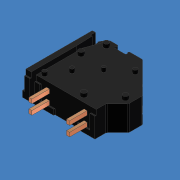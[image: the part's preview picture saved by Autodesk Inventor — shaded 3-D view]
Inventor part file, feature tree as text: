
AUTODESK INVENTOR PART (.ipt)
format: ipt  version: 2012 (Build 160160000, 160)  size: 268,800 bytes
history: native  units: mm (DEFAULTED — no unit token found)
features: sketch x21, extrude x18, revolve x2, pattern_linear x2
ambient origin geometry x8: Origin, YZ Plane, XZ Plane, XY Plane, X Axis, Y Axis, Z Axis, Center Point
bodies: Solid1 (feature_tree)
feature tree (43):
  extrude  "Extrusion1"  Depth=10.0mm TaperAngle=0.0deg
  extrude  "Extrusion2"  Depth=8.8mm TaperAngle=0.0deg
  extrude  "Extrusion3"  Depth=1.5mm TaperAngle=0.0deg
  extrude  "Extrusion4"  Depth=1.5mm TaperAngle=0.0deg
  extrude  "Extrusion5"  Depth=1.5mm TaperAngle=0.0deg
  extrude  "Extrusion6"  Depth=1.5mm TaperAngle=0.0deg
  extrude  "Extrusion7"  Depth=6.3mm TaperAngle=0.0deg
  extrude  "Extrusion8"  TaperAngle=360.0deg  [1 undecoded]
  extrude  "Extrusion9"  TaperAngle=360.0deg  [1 undecoded]
  extrude  "Extrusion10"  Depth=20.0mm TaperAngle=0.0deg
  extrude  "Extrusion11"  Depth=20.0mm TaperAngle=0.0deg
  extrude  "Extrusion12"  [1 undecoded]
  extrude  "Extrusion13"  [1 undecoded]
  extrude  "Extrusion14"  [1 undecoded]
  extrude  "Extrusion15"  [1 undecoded]
  revolve  "Revolution1"  [1 undecoded]
  extrude  "Extrusion16"  [1 undecoded]
  revolve  "Revolution2"  [1 undecoded]
  extrude  "Extrusion17"  [1 undecoded]
  pattern_linear  "Rectangular Pattern1"  [2 undecoded]
  extrude  "Extrusion18"  [1 undecoded]
  pattern_linear  "Rectangular Pattern2"  [2 undecoded]
  sketch  "Sketch21"
  sketch  "Skizze_1"  dims[d0=10.0mm d1=0.0mm d2=10.0mm d3=0.0mm]
  sketch  "Skizze_2"  dims[d4=2.4mm d5=0.0mm d6=8.8mm d7=0.0mm]
  sketch  "Skizze_4"  dims[d12=1.5mm d13=0.0mm d14=1.5mm d15=0.0mm]
  sketch  "Skizze_3"  dims[d8=7.6mm d9=0.0mm d10=1.5mm d11=0.0mm]
  sketch  "Skizze_5"  dims[d16=1.5mm d17=0.0mm d18=1.5mm d19=0.0mm]
  sketch  "Skizze_8"  dims[d28=0.5mm d29=0.0mm d30=360.0deg]
  sketch  "Skizze_9"  dims[d31=6.5mm d32=0.0mm d33=360.0deg]
  sketch  "Skizze_10"  dims[d34=13.0mm d35=0.0mm d36=20.0mm d38=15.0mm d39=10.0mm d41=0.0mm]
  sketch  "Skizze_11"  dims[d42=13.0mm d43=0.0mm d44=20.0mm d46=15.0mm d47=10.0mm d49=0.0mm]
  sketch  "Skizze_12"
  sketch  "Skizze_13"
  sketch  "Skizze_14"
  sketch  "Skizze_15"
  sketch  "Skizze_6"  dims[d20=1.5mm d21=0.0mm d22=1.5mm d23=0.0mm]
  sketch  "Skizze_7"  dims[d24=1.5mm d25=0.0mm d26=6.3mm d27=0.0mm]
  sketch  "Skizze_16"
  sketch  "Skizze_17"
  sketch  "Skizze_18"
  sketch  "Skizze_19"
  sketch  "Skizze_21"
note: 15 required parameter values undecoded (feature->parameter linkage not recoverable at this tier; creation-order binding heuristic only, values carry confidence <= 0.55)
